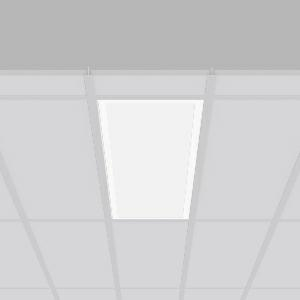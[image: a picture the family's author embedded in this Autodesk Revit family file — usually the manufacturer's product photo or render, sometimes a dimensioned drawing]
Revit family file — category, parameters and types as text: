
# Revit family: sidelite_eco_312367_002_1_76_b1e7
name_source: partatom
category: Lighting Fixtures
units: mm (PartAtom-declared; Revit-internal decimal feet)

## family parameters
Cut with Voids When Loaded = No
Host = Face
Light Source = No
Part Type = Normal
Room Calculation Point = No
Round Connector Dimension = Use Diameter
Shared = No

## types (1)
- MultiLumen 1 (1 x LED Modul 840, 3500 lm, 4000)
    Apparent Load = 29 VA
    CIE Flux Codes = 47 79 96 100 100
    Color Rendering = 80
    Color Temperature = 4000
    Default Elevation = 1800 mm
    Description = Series: SIDELITE ECO
Highly economical recessed luminaire with progressive LED technology. Frame made of aluminium, powder-coated. Diffuser: plastic, opal. Lightguide and diffuser made of non-yellowing plastic (PMMA). Lateral light emission (RZB SIDELITE technology) for homogeneous light distribution. External driver. External driver with simple plug-in locking system and extended converter connecting cable to luminaire (1.90 m). MultiLumen: 4 steps adjustable luminous flux. Factory setting is the lowest offered step. Luminaire can be used with accessories (to be ordered separately) as recessed or surface mounting luminaire. Qualified for use in the food and drink industry. 
Colour: white
Length: 1245 mm
Width: 308 mm
Cut-out length: 1233 mm
Cut-out width: 296 mm
Recess height: 160 mm
Luminaire: recess height: 38 mm
Lamp: LED
Socket: without socket
Colour temperature: 4000K
Colour rendering index (CRI): 80
System power: 29 W
Rated luminous flux: 3500 lm
Luminous efficiency: 121 lm/W
System power 2: 33 W
Rated luminous flux 2: 3850 lm
Luminous efficiency 2: 117 lm/W
System power 3: 35 W
Rated luminous flux 3: 4050 lm
Luminous efficiency 3: 116 lm/W
System power 4: 38 W
Rated luminous flux 4: 4400 lm
Luminous efficiency 4: 116 lm/W
Control gear: Converter, dimmable, DALI
Protection class: II
Type of protection: IP 40
    Height = 0 mm  [stored 0 ft]
    Lamp = 1 x LED Modul 840
    Lamp Light Flux = 3500 lm
    Lamp count = 1
    Length = 1245 mm
    Lifetime = 50000 h
    Luminous efficacy = 121 lm/W
    Manufacturer = RZB
    ModVariant = No
    Model = 312367.002.1.76
    Mounting Place = Ceiling
    Mounting Type = Recessed
    Number of Poles = 1
    OnlyDefault = Yes
    Power Factor = 1
    Product Name = SIDELITE ECO
    Product group = Recessed modular luminaires
    ProductGroupID = 406
    Protection Class = Protection class II
    Protection Degree = IP 20
    RLX_Detail_Level = 1
    RLX_Emergency_Light_Flux = 0 lm
    RLX_Emergency_Type = 0
    RLX_Emergency_Type_DB = No
    RlxData = <blob elided: 31533 chars, md5=60beb58c>
    Socket = socket
    Standby Power = 0 W
    System Light Flux = 3500 lm
    System Power = 29 W
    Type Comments = MultiLumen 1
    Type Image = 312367.002.jpg
    URL = http://relux.com
    VarID = multilumen_1
    Voltage = 230 V
    Voltage Range = 220-240 V
    Weight = 0.00 kg
    Width = 308 mm

note: [stored X ft] marks values corroborated as IEEE doubles in the binary element streams (Revit-internal decimal feet)

## geometry (parser evidence)
native form markers: Blend x4, Sweep x10
no freeform markers — native parametric forms only
